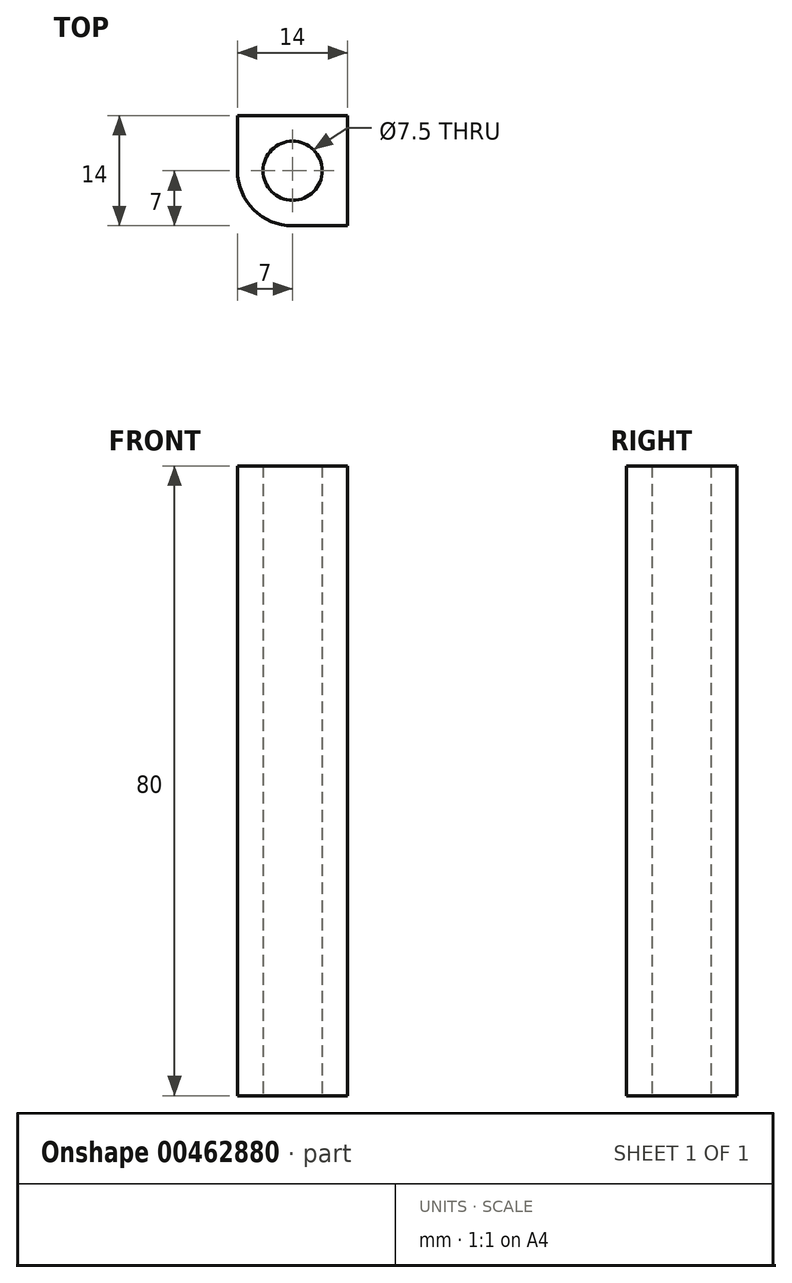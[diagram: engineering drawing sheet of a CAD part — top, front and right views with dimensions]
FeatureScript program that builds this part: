
annotation { "Feature Type Name" : "Feature", "Feature Type Description" : "" }
export const myFeature = defineFeature(function(context is Context, id is Id, definition is map)
    precondition{}
    {
        {
            var Q0;
            Q0=qCreatedBy(makeId("Top.planeOp"),FACE);
            var sketch = newSketch(context, id + "F0", { "sketchPlane" : qUnion([Q0])});
            skLineSegment(sketch, "E0.bottom", {"start": v(-7, 7) * mm, "end": v(7, 7) * mm});
            skLineSegment(sketch, "E0.top", {"start": v(-7, -7) * mm, "end": v(7, -7) * mm});
            skLineSegment(sketch, "E0.left", {"start": v(-7, 7) * mm, "end": v(-7, -7) * mm});
            skLineSegment(sketch, "E0.right", {"start": v(7, 7) * mm, "end": v(7, -7) * mm});
            skPoint(sketch, "E0.middle", {"position": v(0, 0) * mm});
            skCircle(sketch, "E1", {"center": v(0, 0) * mm, "radius": 3.75 * mm});
            skSolve(sketch);
        }
        {
            var Q0;
            Q0 = qSketchRegion(id + "F0", true);
            extrude(context, id + "F1", {"entities" : qUnion([Q0]), "depth" : 70 * mm});
        }
        {
            var Q0;
            Q0=makeQuery(id+"F1.opExtrude","CAP_FACE",FACE,{"disambiguationData":[OSD([sQuery(id+"F0.wireOp",EDGE,"E0.bottom"),sQuery(id+"F0.wireOp",EDGE,"E0.top"),sQuery(id+"F0.wireOp",EDGE,"E0.left"),sQuery(id+"F0.wireOp",EDGE,"E0.right"),sQuery(id+"F0.wireOp",EDGE,"E1")])],"isStart":false});
            extrude(context, id + "F2", {"entities" : qUnion([Q0]), "operationType" : NewBodyOperationType.ADD, "depth" : 10 * mm});
        }
        {
            var Q0;
            {var subQ0=sQuery(id+"F0.wireOp",EDGE,"E0.left");var subQ1=sQuery(id+"F0.wireOp",EDGE,"E0.top");Q0=makeQuery(id+"F2.boolean.opBoolean","MERGE",EDGE,{"derivedFrom":[makeQuery(id+"F1.opExtrude","SWEPT_EDGE",EDGE,{"disambiguationData":[OSD([subQ1,subQ0])]}),makeQuery(id+"F2.opExtrude","SWEPT_EDGE",EDGE,{"disambiguationData":[OSD([subQ1,subQ0])]})]});}
            fillet(context, id + "F3", {"entities" : qUnion([Q0]), "radius" : 7 * mm, "tangentPropagation" : true, "allowEdgeOverflow" : false});
        }
    });
